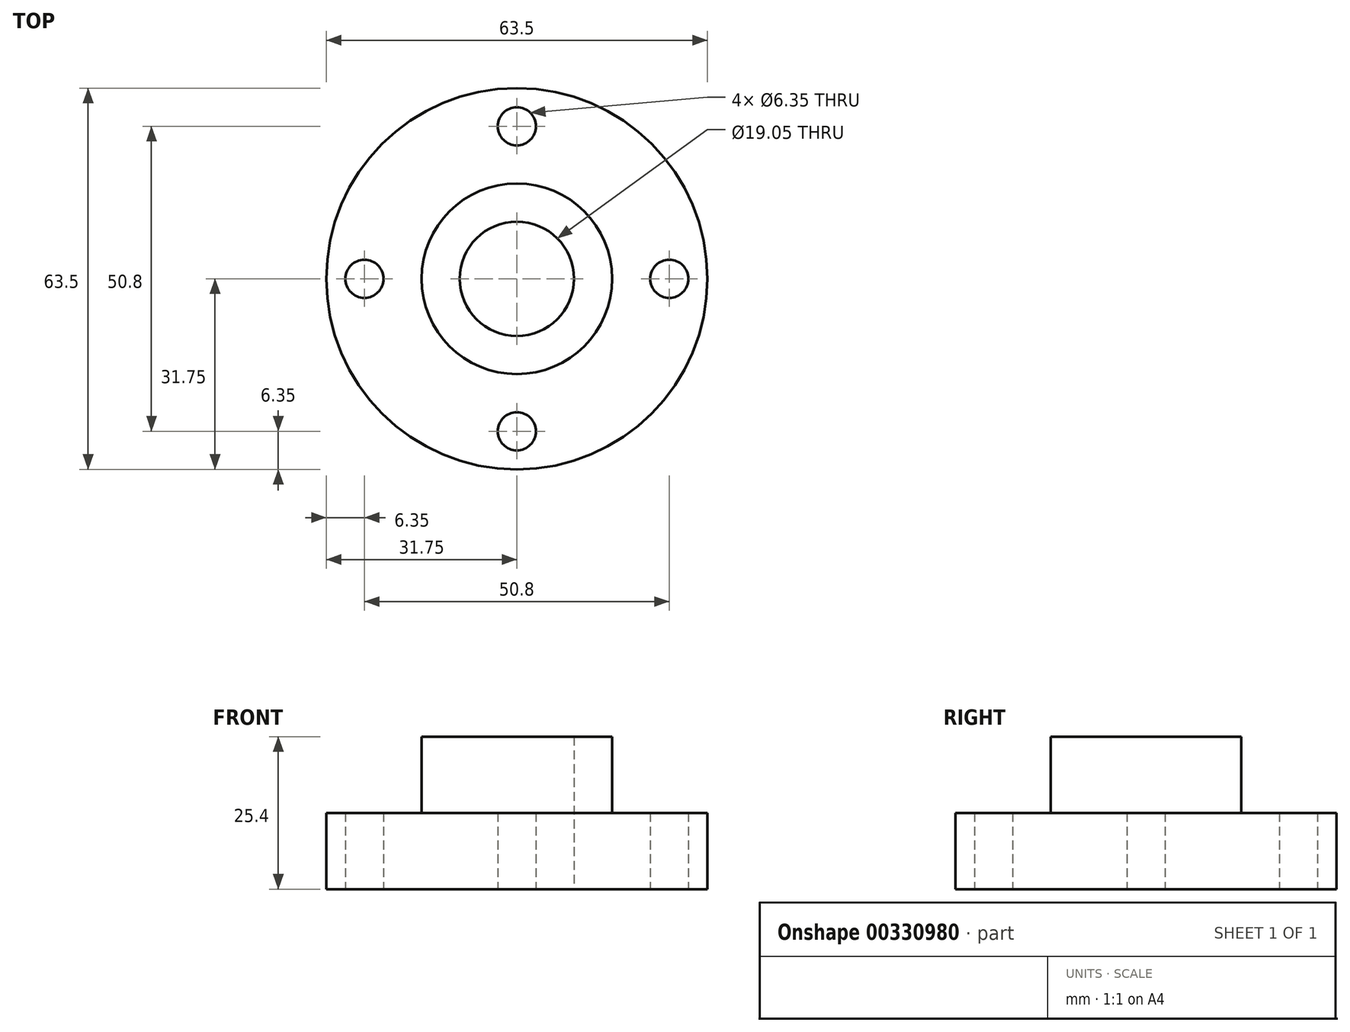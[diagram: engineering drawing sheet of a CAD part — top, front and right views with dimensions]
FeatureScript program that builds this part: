
annotation { "Feature Type Name" : "Feature", "Feature Type Description" : "" }
export const myFeature = defineFeature(function(context is Context, id is Id, definition is map)
    precondition{}
    {
        {
            var Q0;
            Q0=qCreatedBy(makeId("Top.planeOp"),FACE);
            var sketch = newSketch(context, id + "F0", { "sketchPlane" : qUnion([Q0])});
            skCircle(sketch, "E0", {"center": v(0, 0) * mm, "radius": 9.53 * mm});
            skCircle(sketch, "E1", {"center": v(0, 0) * mm, "radius": 15.88 * mm});
            skCircle(sketch, "E2", {"center": v(0, 0) * mm, "radius": 25.4 * mm, "construction": true});
            skCircle(sketch, "E3", {"center": v(0, 0) * mm, "radius": 31.75 * mm});
            skCircle(sketch, "E4", {"center": v(0, 25.4) * mm, "radius": 3.18 * mm});
            skCircle(sketch, "E5", {"center": v(25.4, 0) * mm, "radius": 3.18 * mm});
            skCircle(sketch, "E6", {"center": v(0, -25.4) * mm, "radius": 3.18 * mm});
            skCircle(sketch, "E7", {"center": v(-25.4, 0) * mm, "radius": 3.18 * mm});
            skSolve(sketch);
        }
        {
            var Q0;
            Q0 = qSketchRegion(id + "F0", true);
            extrude(context, id + "F1", {"entities" : qUnion([Q0]), "depth" : 12.7 * mm});
        }
        {
            var Q0;
            Q0=makeQuery(id+"F0.imprint","IMPRINT",FACE,{"disambiguationData":[TD([[makeQuery(id+"F0.imprint","IMPRINT",EDGE,{"derivedFrom":sQuery(id+"F0.wireOp",EDGE,"E0")}),-1.0]])]});
            extrude(context, id + "F2", {"entities" : qUnion([Q0]), "operationType" : NewBodyOperationType.ADD, "depth" : 25.4 * mm});
        }
    });
